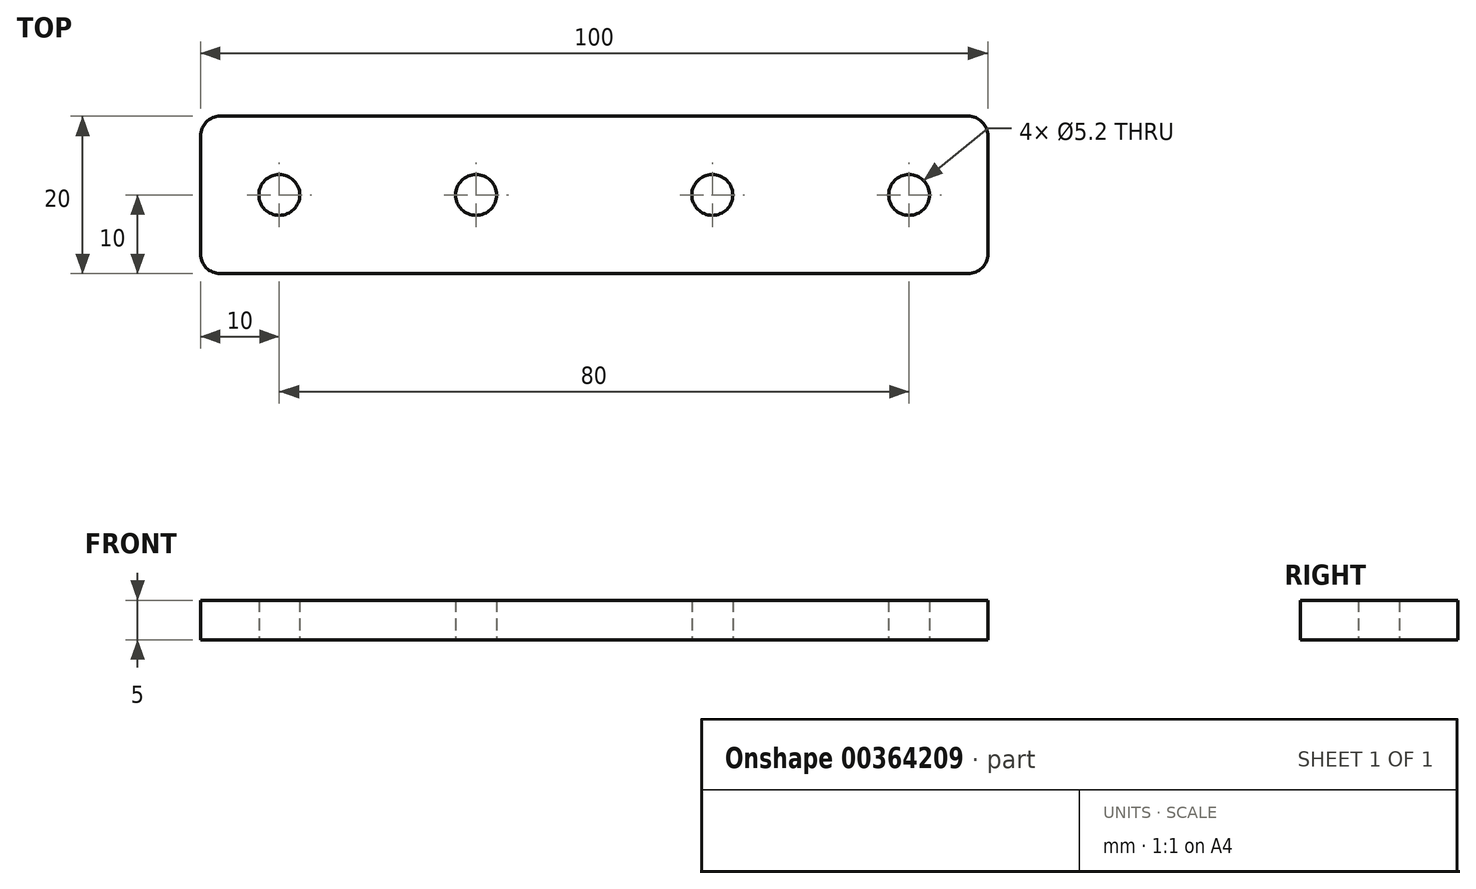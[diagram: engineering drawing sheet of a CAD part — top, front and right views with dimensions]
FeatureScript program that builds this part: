
annotation { "Feature Type Name" : "Feature", "Feature Type Description" : "" }
export const myFeature = defineFeature(function(context is Context, id is Id, definition is map)
    precondition{}
    {
        {
            var Q0;
            Q0=qCreatedBy(makeId("Top.planeOp"),FACE);
            var sketch = newSketch(context, id + "F0", { "sketchPlane" : qUnion([Q0])});
            skLineSegment(sketch, "E0.bottom", {"start": v(47.5, -10) * mm, "end": v(-47.5, -10) * mm});
            skLineSegment(sketch, "E0.top", {"start": v(47.5, 10) * mm, "end": v(-47.5, 10) * mm});
            skLineSegment(sketch, "E0.left", {"start": v(50, -7.5) * mm, "end": v(50, 7.5) * mm});
            skLineSegment(sketch, "E0.right", {"start": v(-50, -7.5) * mm, "end": v(-50, 7.5) * mm});
            skPoint(sketch, "E0.middle", {"position": v(0, 0) * mm});
            skPoint(sketch, "E1.visualSharp", {"position": v(-50, 10) * mm});
            skArc(sketch, "E1.filletArc", {"start": v(-47.5, 10) * mm, "mid": v(-49.27, 9.27) * mm, "end": v(-50, 7.5) * mm});
            skPoint(sketch, "E2.visualSharp", {"position": v(-50, -10) * mm});
            skArc(sketch, "E2.filletArc", {"start": v(-50, -7.5) * mm, "mid": v(-49.27, -9.27) * mm, "end": v(-47.5, -10) * mm});
            skPoint(sketch, "E3.visualSharp", {"position": v(50, -10) * mm});
            skArc(sketch, "E3.filletArc", {"start": v(47.5, -10) * mm, "mid": v(49.27, -9.27) * mm, "end": v(50, -7.5) * mm});
            skPoint(sketch, "E4.visualSharp", {"position": v(50, 10) * mm});
            skArc(sketch, "E4.filletArc", {"start": v(50, 7.5) * mm, "mid": v(49.27, 9.27) * mm, "end": v(47.5, 10) * mm});
            skLineSegment(sketch, "E5", {"start": v(-50, 0) * mm, "end": v(50, 0) * mm, "construction": true});
            skCircle(sketch, "E6", {"center": v(-40, 0) * mm, "radius": 2.6 * mm});
            skCircle(sketch, "E7", {"center": v(-15, 0) * mm, "radius": 2.6 * mm});
            skCircle(sketch, "E8", {"center": v(15, 0) * mm, "radius": 2.6 * mm});
            skCircle(sketch, "E9", {"center": v(40, 0) * mm, "radius": 2.6 * mm});
            skSolve(sketch);
        }
        {
            var Q0;
            Q0=makeQuery(id+"F0.imprint","IMPRINT",FACE,{"disambiguationData":[TD([[makeQuery(id+"F0.imprint","IMPRINT",EDGE,{"derivedFrom":sQuery(id+"F0.wireOp",EDGE,"E0.bottom")}),-1.0]])]});
            extrude(context, id + "F1", {"entities" : qUnion([Q0]), "depth" : 5 * mm});
        }
    });
